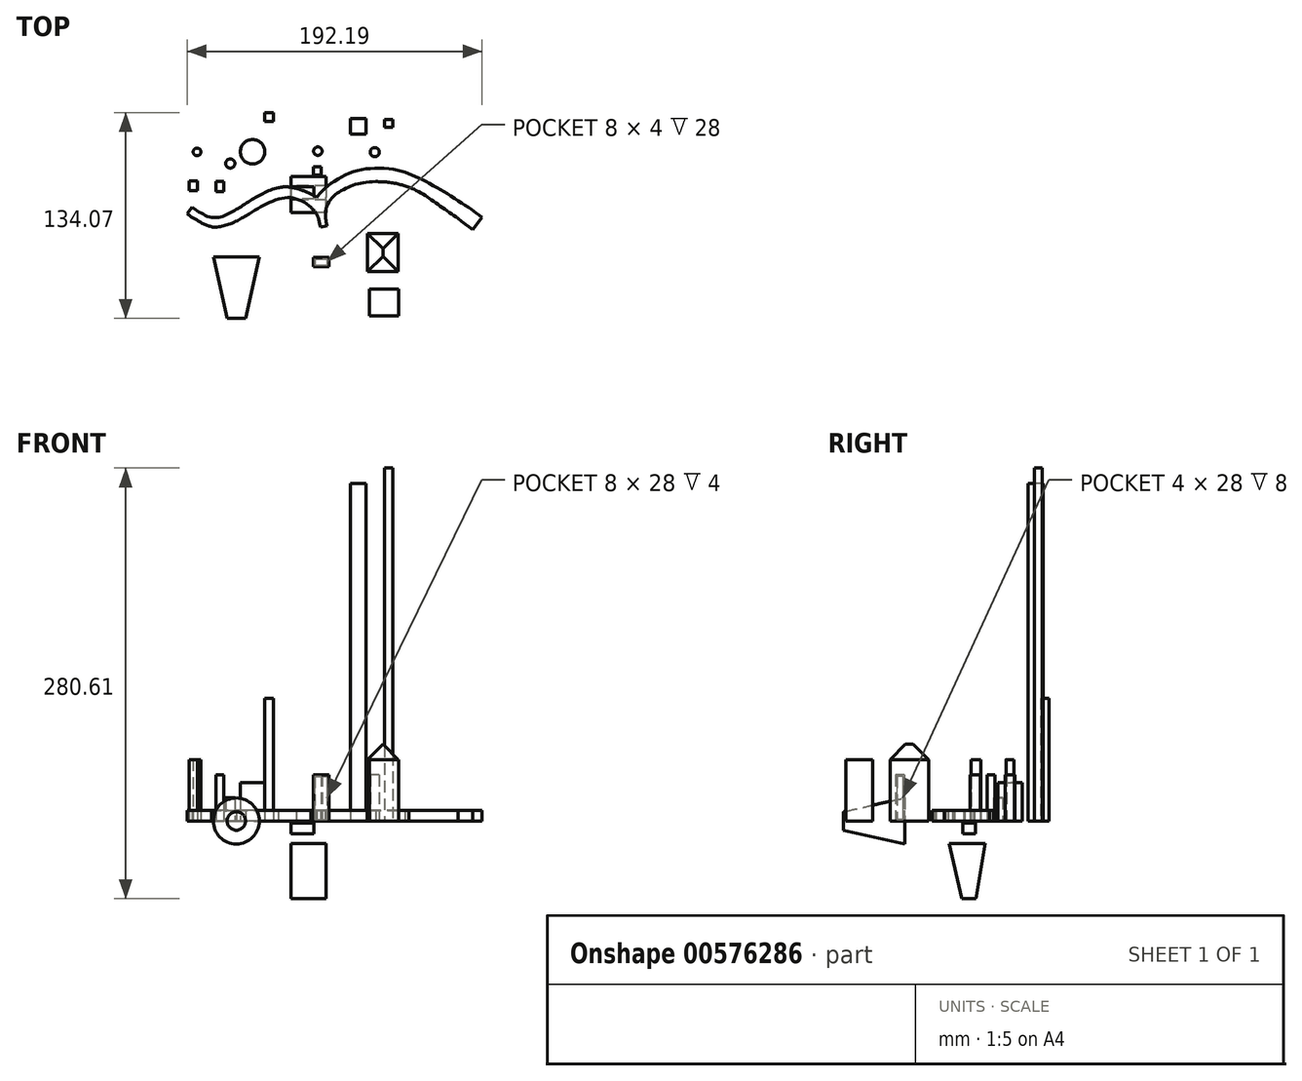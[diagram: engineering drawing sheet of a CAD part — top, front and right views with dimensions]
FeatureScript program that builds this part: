
annotation { "Feature Type Name" : "Feature", "Feature Type Description" : "" }
export const myFeature = defineFeature(function(context is Context, id is Id, definition is map)
    precondition{}
    {
        {
            var Q0;
            Q0=qCreatedBy(makeId("Top.planeOp"),FACE);
            var sketch = newSketch(context, id + "F0", { "sketchPlane" : qUnion([Q0])});
            skFitSpline(sketch, "E0", {"points": [v(-64.43, 10.62) * mm, v(-61.37, 8.5) * mm, v(-57.05, 6.02) * mm, v(-52.99, 4.24) * mm, v(-49.46, 3.87) * mm, v(-46.51, 4.14) * mm, v(-43.26, 5.18) * mm, v(-39.43, 7.03) * mm, v(-35.64, 9.24) * mm], "startDerivative": vector(23.74, -17.24) * mm, "endDerivative": vector(28.43, 17.18) * mm});
            skFitSpline(sketch, "E1", {"points": [v(-35.64, 9.24) * mm, v(-32.45, 11.11) * mm, v(-27.93, 13.85) * mm, v(-24.15, 16.37) * mm, v(-20.29, 18.5) * mm, v(-16.16, 20.63) * mm, v(-12.03, 22.23) * mm, v(-8.3, 23.23) * mm], "startDerivative": vector(23.03, 13.53) * mm, "endDerivative": vector(27.62, 6.72) * mm});
            skFitSpline(sketch, "E2", {"points": [v(-8.3, 23.23) * mm, v(-6.3, 23.62) * mm, v(-4.33, 23.89) * mm, v(-1.7, 23.83) * mm, v(0.74, 23.5) * mm, v(3.63, 22.93) * mm], "startDerivative": vector(10.93, 2.19) * mm, "endDerivative": vector(13.38, -2.78) * mm});
            skFitSpline(sketch, "E3", {"points": [v(3.63, 22.93) * mm, v(8.16, 21.42) * mm, v(12.63, 19.5) * mm, v(16.97, 17.11) * mm], "startDerivative": vector(13.56, -4.3) * mm, "endDerivative": vector(12.02, -7.03) * mm});
            skFitSpline(sketch, "E4", {"points": [v(16.97, 17.11) * mm, v(19.15, 19.92) * mm, v(22.56, 23.2) * mm, v(25.53, 25.54) * mm, v(29, 27.88) * mm, v(32.6, 30.09) * mm, v(36.64, 32.17) * mm, v(41.18, 33.87) * mm, v(45.47, 35.07) * mm, v(50.34, 35.7) * mm, v(55.57, 36.02) * mm, v(61.07, 36.02) * mm, v(66.24, 35.33) * mm, v(70.34, 34.5) * mm, v(74.32, 33.5) * mm], "startDerivative": vector(103.44, 132.94) * mm, "endDerivative": vector(58.6, -15.57) * mm});
            skFitSpline(sketch, "E5", {"points": [v(74.32, 33.5) * mm, v(80.72, 30.93) * mm, v(87.03, 27.87) * mm, v(94.9, 23.61) * mm, v(101.49, 19.72) * mm, v(109.09, 14.8) * mm, v(115.48, 10.63) * mm, v(119.84, 7.58) * mm, v(124.52, 4) * mm], "startDerivative": vector(53.35, -20.42) * mm, "endDerivative": vector(42.56, -33.04) * mm});
            skLineSegment(sketch, "E6", {"start": v(124.52, 4) * mm, "end": v(118.46, -3.92) * mm});
            skLineSegment(sketch, "E7", {"start": v(118.46, -3.92) * mm, "end": v(111.37, 1.5) * mm});
            skLineSegment(sketch, "E8", {"start": v(111.37, 1.5) * mm, "end": v(109.12, 3.23) * mm});
            skFitSpline(sketch, "E9", {"points": [v(109.12, 3.23) * mm, v(103.99, 6.8) * mm, v(98.5, 10.57) * mm, v(93.33, 14.28) * mm, v(88.83, 17.31) * mm, v(84.28, 20.3) * mm, v(79.42, 22.65) * mm, v(76.91, 23.61) * mm], "startDerivative": vector(-32.9, 23.18) * mm, "endDerivative": vector(-22.66, 8.28) * mm});
            skFitSpline(sketch, "E10", {"points": [v(76.91, 23.61) * mm, v(72.6, 25.04) * mm, v(68.1, 26.2) * mm, v(62.68, 26.98) * mm, v(59.04, 27.23) * mm, v(55.36, 27.35) * mm], "startDerivative": vector(-21.22, 7.27) * mm, "endDerivative": vector(-20.4, 0.6) * mm});
            skFitSpline(sketch, "E11", {"points": [v(55.36, 27.35) * mm, v(49.32, 26.91) * mm, v(44.83, 26.2) * mm, v(41.01, 25.04) * mm, v(37.41, 23.75) * mm, v(33.77, 21.84) * mm, v(30.57, 20.02) * mm, v(28.4, 18.33) * mm, v(26, 15.93) * mm, v(24, 12.64) * mm, v(23.01, 9.89) * mm], "startDerivative": vector(-49.95, -3.05) * mm, "endDerivative": vector(-9.45, -30.96) * mm});
            skFitSpline(sketch, "E12", {"points": [v(23.01, 9.89) * mm, v(22.77, 8.59) * mm, v(22.65, 7.23) * mm, v(22.63, 5.2) * mm, v(22.68, 3.4) * mm, v(23.01, 1.06) * mm, v(23.57, -1.52) * mm], "startDerivative": vector(-2, -9.42) * mm, "endDerivative": vector(3.02, -13.12) * mm});
            skFitSpline(sketch, "E13", {"points": [v(23.57, -1.52) * mm, v(19.32, -2.41) * mm], "startDerivative": vector(-4.25, -0.89) * mm, "endDerivative": vector(-4.25, -0.89) * mm});
            skFitSpline(sketch, "E14", {"points": [v(19.32, -2.41) * mm, v(18.85, -0.3) * mm, v(18.1, 3.14) * mm, v(17.21, 5.3) * mm, v(15.96, 7.45) * mm, v(14.24, 9.42) * mm, v(13.13, 10.53) * mm], "startDerivative": vector(-2.91, 12.22) * mm, "endDerivative": vector(-7.74, 7.63) * mm});
            skFitSpline(sketch, "E15", {"points": [v(13.13, 10.53) * mm, v(10.55, 12.58) * mm, v(7.56, 14.48) * mm, v(3.62, 16.02) * mm, v(0, 16.82) * mm, v(-3.36, 16.87) * mm, v(-7.3, 16.17) * mm, v(-12.03, 14.58) * mm, v(-15.92, 12.88) * mm, v(-20.15, 10.53) * mm, v(-24.69, 7.85) * mm, v(-29.32, 4.9) * mm], "startDerivative": vector(-31.72, 26.04) * mm, "endDerivative": vector(-44.78, -28.9) * mm});
            skFitSpline(sketch, "E16", {"points": [v(-29.32, 4.9) * mm, v(-31.68, 3.66) * mm, v(-34.9, 1.89) * mm, v(-38.87, 0) * mm, v(-42.66, -1.22) * mm, v(-46.04, -2.02) * mm, v(-48.77, -2.41) * mm, v(-50.07, -2.41) * mm, v(-51.79, -2.11) * mm], "startDerivative": vector(-19.02, -9.88) * mm, "endDerivative": vector(-18.74, 3.78) * mm});
            skFitSpline(sketch, "E17", {"points": [v(-51.79, -2.11) * mm, v(-55.15, -0.92) * mm, v(-59.09, 0.91) * mm, v(-61.82, 2.62) * mm, v(-64.22, 4.01) * mm, v(-67.67, 6.52) * mm], "startDerivative": vector(-16.4, 5.46) * mm, "endDerivative": vector(-16.48, 12.67) * mm});
            skFitSpline(sketch, "E18", {"points": [v(-67.67, 6.52) * mm, v(-64.43, 10.62) * mm], "startDerivative": vector(3.24, 4.1) * mm, "endDerivative": vector(3.24, 4.1) * mm});
            skLineSegment(sketch, "E19", {"start": v(-68.54, -50.32) * mm, "end": v(31.46, -53.62) * mm});
            skSolve(sketch);
        }
        {
            var Q0;
            Q0=makeQuery(id+"F0.imprint","IMPRINT",FACE,{"disambiguationData":[TD([[makeQuery(id+"F0.imprint","IMPRINT",EDGE,{"derivedFrom":sQuery(id+"F0.wireOp",EDGE,"E0")}),-1.0]])]});
            extrude(context, id + "F1", {"entities" : qUnion([Q0]), "flatOperationType" : FlatOperationType.REMOVE, "depth" : 7 * mm, "offsetDistance" : 25 * mm, "domain" : OperationDomain.MODEL});
        }
        {
            var Q0;
            Q0=qCreatedBy(makeId("Top.planeOp"),FACE);
            var sketch = newSketch(context, id + "F2", { "sketchPlane" : qUnion([Q0])});
            skCircle(sketch, "E20", {"center": v(17.58, 47.17) * mm, "radius": 2.75 * mm});
            skSolve(sketch);
        }
        {
            var Q0;
            Q0 = qSketchRegion(id + "F2", true);
            extrude(context, id + "F3", {"entities" : qUnion([Q0]), "depth" : 30 * mm, "offsetDistance" : 25 * mm});
        }
        {
            var Q0;
            Q0=qCreatedBy(makeId("Top.planeOp"),FACE);
            var sketch = newSketch(context, id + "F4", { "sketchPlane" : qUnion([Q0])});
            skCircle(sketch, "E21", {"center": v(-61.12, 46.66) * mm, "radius": 2.5 * mm});
            skSolve(sketch);
        }
        {
            var Q0;
            Q0 = qSketchRegion(id + "F4", true);
            extrude(context, id + "F5", {"entities" : qUnion([Q0]), "depth" : 40 * mm, "offsetDistance" : 25 * mm});
        }
        {
            var Q0;
            Q0=qCreatedBy(makeId("Top.planeOp"),FACE);
            var sketch = newSketch(context, id + "F6", { "sketchPlane" : qUnion([Q0])});
            skLineSegment(sketch, "E22", {"start": v(-50.51, -21.82) * mm, "end": v(-35.51, -21.82) * mm});
            skLineSegment(sketch, "E23", {"start": v(-35.51, -21.82) * mm, "end": v(-35.51, -61.82) * mm});
            skLineSegment(sketch, "E24", {"start": v(-35.51, -61.82) * mm, "end": v(-41.51, -61.82) * mm});
            skLineSegment(sketch, "E25", {"start": v(-41.51, -61.82) * mm, "end": v(-50.51, -21.82) * mm});
            skSolve(sketch);
        }
        {
            var Q0;
            Q0=makeQuery(id+"F6.imprint","IMPRINT",FACE,{"disambiguationData":[TD([[makeQuery(id+"F6.imprint","IMPRINT",EDGE,{"derivedFrom":sQuery(id+"F6.wireOp",EDGE,"E22")}),-1.0]])]});
            var Q1;
            Q1=sQuery(id+"F6.wireOp",EDGE,"E23");
            revolve(context, id + "F7", {"entities" : qUnion([Q0]), "axis" : qUnion([Q1]), "revolveType" : RevolveType.FULL});
        }
        {
            var Q0;
            Q0=qCreatedBy(makeId("Top.planeOp"),FACE);
            var sketch = newSketch(context, id + "F8", { "sketchPlane" : qUnion([Q0])});
            skLineSegment(sketch, "E26.bottom", {"start": v(14.69, -22) * mm, "end": v(24.69, -22) * mm});
            skLineSegment(sketch, "E26.top", {"start": v(14.69, -28) * mm, "end": v(24.69, -28) * mm});
            skLineSegment(sketch, "E26.left", {"start": v(14.69, -22) * mm, "end": v(14.69, -28) * mm});
            skLineSegment(sketch, "E26.right", {"start": v(24.69, -22) * mm, "end": v(24.69, -28) * mm});
            skSolve(sketch);
        }
        {
            var Q0;
            Q0 = qSketchRegion(id + "F8", true);
            extrude(context, id + "F9", {"entities" : qUnion([Q0]), "depth" : 30 * mm, "offsetDistance" : 25 * mm});
        }
        {
            var Q0;
            Q0=makeQuery(id+"F9.opExtrude","SWEPT_FACE",FACE,{"disambiguationData":[OSD([sQuery(id+"F8.wireOp",EDGE,"E26.left")])]});
            var Q1;
            Q1=makeQuery(id+"F9.opExtrude","SWEPT_BODY",BODY,{"disambiguationData":[OSD([sQuery(id+"F8.wireOp",EDGE,"E26.bottom"),sQuery(id+"F8.wireOp",EDGE,"E26.top"),sQuery(id+"F8.wireOp",EDGE,"E26.left"),sQuery(id+"F8.wireOp",EDGE,"E26.right")])]});
            shell(context, id + "F10", {"isHollow" : true, "entities" : qUnion([Q0]), "parts" : qUnion([Q1]), "thickness" : 1 * mm});
        }
        {
            var Q0;
            Q0=qCreatedBy(makeId("Top.planeOp"),FACE);
            var sketch = newSketch(context, id + "F11", { "sketchPlane" : qUnion([Q0])});
            skCircle(sketch, "E27", {"center": v(-39.46, 39.12) * mm, "radius": 3 * mm});
            skSolve(sketch);
        }
        {
            var Q0;
            Q0 = qSketchRegion(id + "F11", true);
            extrude(context, id + "F12", {"entities" : qUnion([Q0]), "depth" : 15 * mm, "offsetDistance" : 25 * mm});
        }
        {
            var Q0;
            Q0=qCreatedBy(makeId("Top.planeOp"),FACE);
            var sketch = newSketch(context, id + "F13", { "sketchPlane" : qUnion([Q0])});
            skCircle(sketch, "E28", {"center": v(-24.94, 46.77) * mm, "radius": 8 * mm});
            skSolve(sketch);
        }
        {
            var Q0;
            Q0 = qSketchRegion(id + "F13", true);
            extrude(context, id + "F14", {"entities" : qUnion([Q0]), "depth" : 25 * mm, "offsetDistance" : 25 * mm});
        }
        {
            var Q0;
            Q0=qCreatedBy(makeId("Top.planeOp"),FACE);
            var sketch = newSketch(context, id + "F15", { "sketchPlane" : qUnion([Q0])});
            skCircle(sketch, "E29", {"center": v(54.68, 46.53) * mm, "radius": 3 * mm});
            skSolve(sketch);
        }
        {
            var Q0;
            Q0 = qSketchRegion(id + "F15", true);
            extrude(context, id + "F16", {"entities" : qUnion([Q0]), "depth" : 30 * mm, "offsetDistance" : 25 * mm});
        }
        {
            var Q0;
            Q0=qCreatedBy(makeId("Top.planeOp"),FACE);
            var sketch = newSketch(context, id + "F17", { "sketchPlane" : qUnion([Q0])});
            skLineSegment(sketch, "E30.bottom", {"start": v(38.95, 68.42) * mm, "end": v(48.95, 68.42) * mm});
            skLineSegment(sketch, "E30.top", {"start": v(38.95, 58.42) * mm, "end": v(48.95, 58.42) * mm});
            skLineSegment(sketch, "E30.left", {"start": v(38.95, 68.42) * mm, "end": v(38.95, 58.42) * mm});
            skLineSegment(sketch, "E30.right", {"start": v(48.95, 68.42) * mm, "end": v(48.95, 58.42) * mm});
            skSolve(sketch);
        }
        {
            var Q0;
            Q0 = qSketchRegion(id + "F17", true);
            extrude(context, id + "F18", {"entities" : qUnion([Q0]), "depth" : 220 * mm, "offsetDistance" : 25 * mm});
        }
        {
            var Q0;
            Q0=qCreatedBy(makeId("Top.planeOp"),FACE);
            var sketch = newSketch(context, id + "F19", { "sketchPlane" : qUnion([Q0])});
            skLineSegment(sketch, "E31.bottom", {"start": v(50.06, -6.4) * mm, "end": v(70.06, -6.4) * mm});
            skLineSegment(sketch, "E31.top", {"start": v(50.06, -31.4) * mm, "end": v(70.06, -31.4) * mm});
            skLineSegment(sketch, "E31.left", {"start": v(50.06, -6.4) * mm, "end": v(50.06, -31.4) * mm});
            skLineSegment(sketch, "E31.right", {"start": v(70.06, -6.4) * mm, "end": v(70.06, -31.4) * mm});
            skSolve(sketch);
        }
        {
            var Q0;
            Q0 = qSketchRegion(id + "F19", true);
            extrude(context, id + "F20", {"entities" : qUnion([Q0]), "depth" : 50 * mm, "offsetDistance" : 25 * mm});
        }
        {
            var Q0;
            Q0=makeQuery(id+"F20.opExtrude","CAP_FACE",FACE,{"disambiguationData":[OSD([sQuery(id+"F19.wireOp",EDGE,"E31.bottom"),sQuery(id+"F19.wireOp",EDGE,"E31.top"),sQuery(id+"F19.wireOp",EDGE,"E31.left"),sQuery(id+"F19.wireOp",EDGE,"E31.right")])],"isStart":false});
            chamfer(context, id + "F21", {"entities" : qUnion([Q0]), "width" : 10 * mm, "tangentPropagation" : true});
        }
        {
            var Q0;
            Q0=qCreatedBy(makeId("Top.planeOp"),FACE);
            var sketch = newSketch(context, id + "F22", { "sketchPlane" : qUnion([Q0])});
            skLineSegment(sketch, "E32.bottom", {"start": v(60.95, 67.66) * mm, "end": v(66.3, 67.66) * mm});
            skLineSegment(sketch, "E32.top", {"start": v(60.95, 62.57) * mm, "end": v(66.3, 62.57) * mm});
            skLineSegment(sketch, "E32.left", {"start": v(60.95, 67.66) * mm, "end": v(60.95, 62.57) * mm});
            skLineSegment(sketch, "E32.right", {"start": v(66.3, 67.66) * mm, "end": v(66.3, 62.57) * mm});
            skSolve(sketch);
        }
        {
            var Q0;
            Q0 = qSketchRegion(id + "F22", true);
            extrude(context, id + "F23", {"entities" : qUnion([Q0]), "depth" : 230 * mm, "offsetDistance" : 25 * mm});
        }
        {
            var Q0;
            Q0=qCreatedBy(makeId("Top.planeOp"),FACE);
            var sketch = newSketch(context, id + "F24", { "sketchPlane" : qUnion([Q0])});
            skLineSegment(sketch, "E33.bottom", {"start": v(51.26, -42.69) * mm, "end": v(70.12, -42.69) * mm});
            skLineSegment(sketch, "E33.top", {"start": v(51.26, -60.27) * mm, "end": v(70.12, -60.27) * mm});
            skLineSegment(sketch, "E33.left", {"start": v(51.26, -42.69) * mm, "end": v(51.26, -60.27) * mm});
            skLineSegment(sketch, "E33.right", {"start": v(70.12, -42.69) * mm, "end": v(70.12, -60.27) * mm});
            skSolve(sketch);
        }
        {
            var Q0;
            Q0 = qSketchRegion(id + "F24", true);
            extrude(context, id + "F25", {"entities" : qUnion([Q0]), "depth" : 40 * mm, "offsetDistance" : 25 * mm});
        }
        {
            var Q0;
            Q0=qCreatedBy(makeId("Top.planeOp"),FACE);
            var sketch = newSketch(context, id + "F26", { "sketchPlane" : qUnion([Q0])});
            skLineSegment(sketch, "E34.bottom", {"start": v(-17.04, 72.25) * mm, "end": v(-11.43, 72.25) * mm});
            skLineSegment(sketch, "E34.top", {"start": v(-17.04, 66.64) * mm, "end": v(-11.43, 66.64) * mm});
            skLineSegment(sketch, "E34.left", {"start": v(-17.04, 72.25) * mm, "end": v(-17.04, 66.64) * mm});
            skLineSegment(sketch, "E34.right", {"start": v(-11.43, 72.25) * mm, "end": v(-11.43, 66.64) * mm});
            skSolve(sketch);
        }
        {
            var Q0;
            Q0 = qSketchRegion(id + "F26", true);
            extrude(context, id + "F27", {"entities" : qUnion([Q0]), "depth" : 80 * mm, "offsetDistance" : 25 * mm});
        }
        {
            var Q0;
            Q0=qCreatedBy(makeId("Top.planeOp"),FACE);
            var sketch = newSketch(context, id + "F28", { "sketchPlane" : qUnion([Q0])});
            skLineSegment(sketch, "E35.bottom", {"start": v(14.57, 37.08) * mm, "end": v(19.92, 37.08) * mm});
            skLineSegment(sketch, "E35.top", {"start": v(14.57, 31.73) * mm, "end": v(19.92, 31.73) * mm});
            skLineSegment(sketch, "E35.left", {"start": v(14.57, 37.08) * mm, "end": v(14.57, 31.73) * mm});
            skLineSegment(sketch, "E35.right", {"start": v(19.92, 37.08) * mm, "end": v(19.92, 31.73) * mm});
            skSolve(sketch);
        }
        {
            var Q0;
            Q0 = qSketchRegion(id + "F28", true);
            extrude(context, id + "F29", {"entities" : qUnion([Q0]), "depth" : 30 * mm, "offsetDistance" : 25 * mm});
        }
        {
            var Q0;
            Q0=qCreatedBy(makeId("Top.planeOp"),FACE);
            var sketch = newSketch(context, id + "F30", { "sketchPlane" : qUnion([Q0])});
            skLineSegment(sketch, "E36.bottom", {"start": v(-48.77, 27.4) * mm, "end": v(-43.67, 27.4) * mm});
            skLineSegment(sketch, "E36.top", {"start": v(-48.77, 20.77) * mm, "end": v(-43.67, 20.77) * mm});
            skLineSegment(sketch, "E36.left", {"start": v(-48.77, 27.4) * mm, "end": v(-48.77, 20.77) * mm});
            skLineSegment(sketch, "E36.right", {"start": v(-43.67, 27.4) * mm, "end": v(-43.67, 20.77) * mm});
            skSolve(sketch);
        }
        {
            var Q0;
            Q0 = qSketchRegion(id + "F30", true);
            extrude(context, id + "F31", {"entities" : qUnion([Q0]), "depth" : 30 * mm, "offsetDistance" : 25 * mm});
        }
        {
            var Q0;
            Q0=qCreatedBy(makeId("Top.planeOp"),FACE);
            var sketch = newSketch(context, id + "F32", { "sketchPlane" : qUnion([Q0])});
            skLineSegment(sketch, "E37.bottom", {"start": v(-39.46, 26.95) * mm, "end": v(-34.63, 26.95) * mm});
            skLineSegment(sketch, "E37.top", {"start": v(-39.46, 19.95) * mm, "end": v(-34.63, 19.95) * mm});
            skLineSegment(sketch, "E37.left", {"start": v(-39.46, 26.95) * mm, "end": v(-39.46, 19.95) * mm});
            skLineSegment(sketch, "E37.right", {"start": v(-34.63, 26.95) * mm, "end": v(-34.63, 19.95) * mm});
            skSolve(sketch);
        }
        {
            var Q0;
            Q0=qCreatedBy(makeId("Top.planeOp"),FACE);
            var sketch = newSketch(context, id + "F33", { "sketchPlane" : qUnion([Q0])});
            skLineSegment(sketch, "E38.bottom", {"start": v(-66.35, 27.65) * mm, "end": v(-60.74, 27.65) * mm});
            skLineSegment(sketch, "E38.top", {"start": v(-66.35, 21.28) * mm, "end": v(-60.74, 21.28) * mm});
            skLineSegment(sketch, "E38.left", {"start": v(-66.35, 27.65) * mm, "end": v(-66.35, 21.28) * mm});
            skLineSegment(sketch, "E38.right", {"start": v(-60.74, 27.65) * mm, "end": v(-60.74, 21.28) * mm});
            skSolve(sketch);
        }
        {
            var Q0;
            Q0 = qSketchRegion(id + "F33", true);
            extrude(context, id + "F34", {"entities" : qUnion([Q0]), "depth" : 40 * mm, "offsetDistance" : 25 * mm});
        }
        {
            var Q0;
            Q0=qCreatedBy(makeId("Right.planeOp"),FACE);
            var sketch = newSketch(context, id + "F35", { "sketchPlane" : qUnion([Q0])});
            skLineSegment(sketch, "E39.bottom", {"start": v(16.12, -1.4) * mm, "end": v(24.12, -1.4) * mm});
            skLineSegment(sketch, "E39.top", {"start": v(16.12, -8.4) * mm, "end": v(24.12, -8.4) * mm});
            skLineSegment(sketch, "E39.left", {"start": v(16.12, -1.4) * mm, "end": v(16.12, -8.4) * mm});
            skLineSegment(sketch, "E39.right", {"start": v(24.12, -1.4) * mm, "end": v(24.12, -8.4) * mm});
            skSolve(sketch);
        }
        {
            var Q0;
            Q0 = qSketchRegion(id + "F35", true);
            extrude(context, id + "F36", {"entities" : qUnion([Q0]), "depth" : 15 * mm, "offsetDistance" : 25 * mm});
        }
        {
            var Q0;
            Q0=qCreatedBy(makeId("Right.planeOp"),FACE);
            var sketch = newSketch(context, id + "F37", { "sketchPlane" : qUnion([Q0])});
            skLineSegment(sketch, "E40", {"start": v(7.01, -14.78) * mm, "end": v(30.63, -14.78) * mm});
            skLineSegment(sketch, "E41", {"start": v(30.63, -14.78) * mm, "end": v(24.56, -50.6) * mm});
            skLineSegment(sketch, "E42", {"start": v(24.56, -50.6) * mm, "end": v(15.44, -50.6) * mm});
            skLineSegment(sketch, "E43", {"start": v(15.44, -50.6) * mm, "end": v(7.01, -14.78) * mm});
            skSolve(sketch);
        }
        {
            var Q0;
            Q0 = qSketchRegion(id + "F37", true);
            extrude(context, id + "F38", {"entities" : qUnion([Q0]), "depth" : 23 * mm, "offsetDistance" : 25 * mm});
        }
    });
